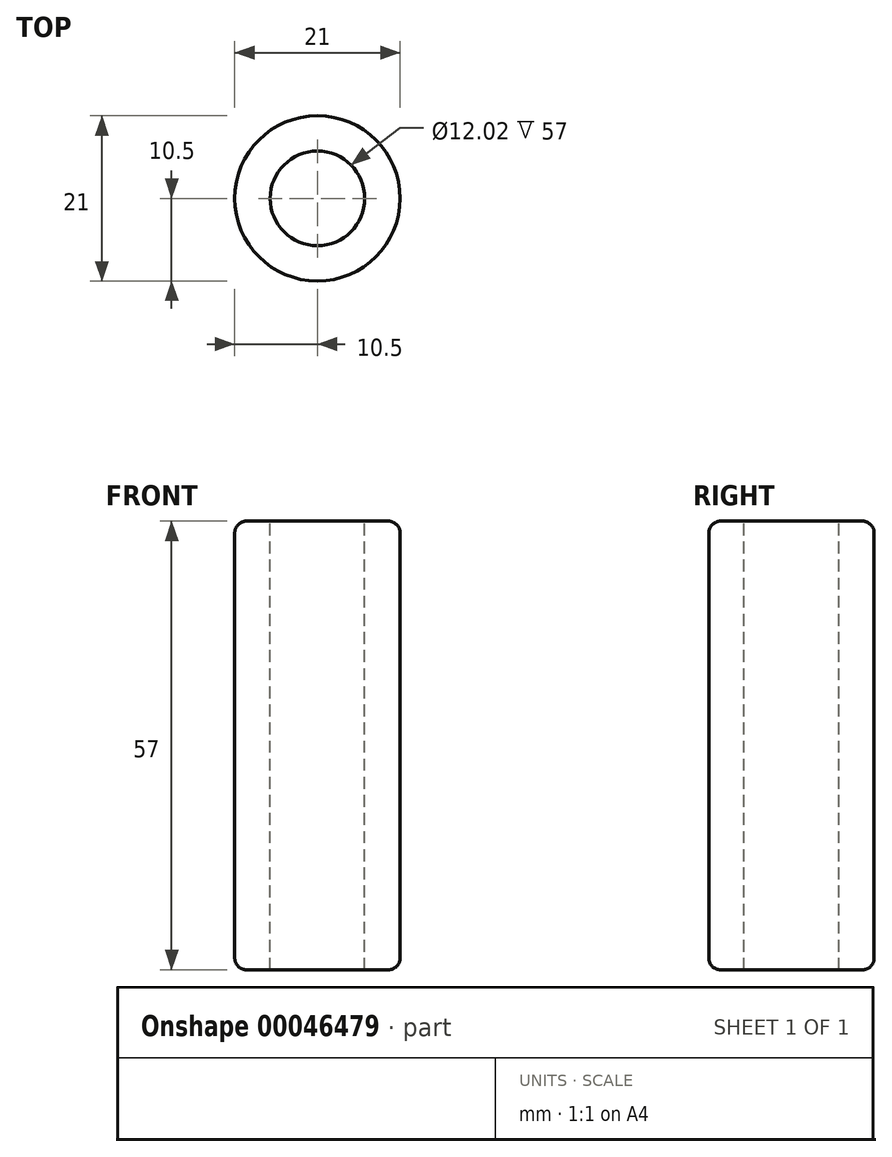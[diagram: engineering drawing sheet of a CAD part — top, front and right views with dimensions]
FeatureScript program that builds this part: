
annotation { "Feature Type Name" : "Feature", "Feature Type Description" : "" }
export const myFeature = defineFeature(function(context is Context, id is Id, definition is map)
    precondition{}
    {
        {
            var Q0;
            Q0=qCreatedBy(makeId("Top.planeOp"),FACE);
            var sketch = newSketch(context, id + "F0", { "sketchPlane" : qUnion([Q0])});
            skCircle(sketch, "E0", {"center": v(0, 0) * mm, "radius": 10.5 * mm});
            skSolve(sketch);
        }
        {
            var Q0;
            Q0 = qSketchRegion(id + "F0", true);
            extrude(context, id + "F1", {"entities" : qUnion([Q0]), "depth" : 57 * mm});
        }
        {
            var Q0;
            Q0=makeQuery(id+"F1.opExtrude","CAP_FACE",FACE,{"disambiguationData":[OSD([sQuery(id+"F0.wireOp",EDGE,"E0")])],"isStart":false});
            var sketch = newSketch(context, id + "F2", { "sketchPlane" : qUnion([Q0])});
            skCircle(sketch, "E1", {"center": v(0, 0) * mm, "radius": 6 * mm});
            skSolve(sketch);
        }
        {
            var Q0;
            Q0 = qSketchRegion(id + "F2", true);
            extrude(context, id + "F3", {"entities" : qUnion([Q0]), "operationType" : NewBodyOperationType.REMOVE, "endBound" : BoundingType.THROUGH_ALL, "oppositeDirection" : true, "depth" : 25 * mm});
        }
        {
            var Q0;
            Q0=makeQuery(id+"F1.opExtrude","CAP_EDGE",EDGE,{"disambiguationData":[OSD([sQuery(id+"F0.wireOp",EDGE,"E0")])],"isStart":false});
            var Q1;
            Q1=makeQuery(id+"F1.opExtrude","CAP_EDGE",EDGE,{"disambiguationData":[OSD([sQuery(id+"F0.wireOp",EDGE,"E0")])],"isStart":true});
            fillet(context, id + "F4", {"entities" : qUnion([Q0, Q1]), "radius" : 1.5 * mm, "tangentPropagation" : true, "allowEdgeOverflow" : false});
        }
    });
